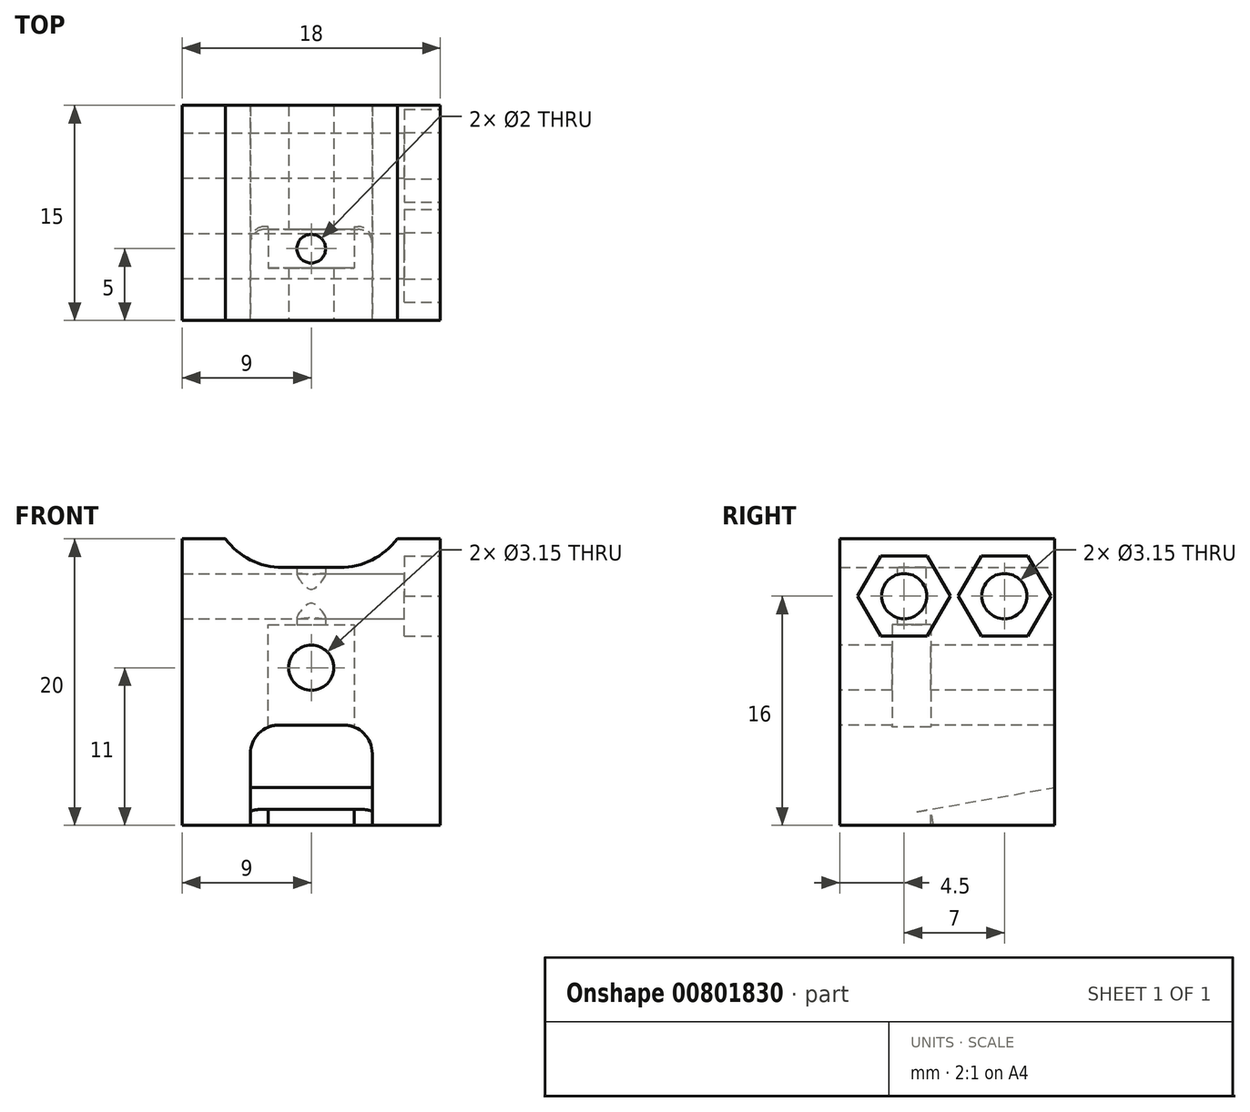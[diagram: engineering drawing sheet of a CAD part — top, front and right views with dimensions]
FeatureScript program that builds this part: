
annotation { "Feature Type Name" : "Feature", "Feature Type Description" : "" }
export const myFeature = defineFeature(function(context is Context, id is Id, definition is map)
    precondition{}
    {
        {
            var Q0;
            Q0=qCreatedBy(makeId("Front.planeOp"),FACE);
            var sketch = newSketch(context, id + "F0", { "sketchPlane" : qUnion([Q0])});
            skLineSegment(sketch, "E0.bottom", {"start": v(0, 0) * mm, "end": v(18, 0) * mm});
            skLineSegment(sketch, "E0.top", {"start": v(0, 20) * mm, "end": v(18, 20) * mm});
            skLineSegment(sketch, "E0.left", {"start": v(0, 0) * mm, "end": v(0, 20) * mm});
            skLineSegment(sketch, "E0.right", {"start": v(18, 0) * mm, "end": v(18, 20) * mm});
            skSolve(sketch);
        }
        {
            var Q0;
            Q0=makeQuery(id+"F0.imprint","IMPRINT",FACE,{"disambiguationData":[TD([[makeQuery(id+"F0.imprint","IMPRINT",EDGE,{"derivedFrom":sQuery(id+"F0.wireOp",EDGE,"E0.bottom")}),1.0]])]});
            extrude(context, id + "F1", {"entities" : qUnion([Q0]), "depth" : 15 * mm, "offsetDistance" : 25 * mm});
        }
        {
            var Q0;
            Q0=makeQuery(id+"F1.opExtrude","SWEPT_FACE",FACE,{"disambiguationData":[OSD([sQuery(id+"F0.wireOp",EDGE,"E0.right")])]});
            var sketch = newSketch(context, id + "F2", { "sketchPlane" : qUnion([Q0])});
            skPoint(sketch, "E1", {"position": v(-10.5, 16) * mm});
            skPoint(sketch, "E2", {"position": v(-3.5, 16) * mm});
            skSolve(sketch);
        }
        {
            var Q0;
            Q0=sQuery(id+"F2.wireOp",VERTEX,"E2");
            var Q1;
            Q1=sQuery(id+"F2.wireOp",VERTEX,"E1");
            var Q2;
            Q2=makeQuery(id+"F1.opExtrude","SWEPT_BODY",BODY,{"disambiguationData":[OSD([sQuery(id+"F0.wireOp",EDGE,"E0.bottom"),sQuery(id+"F0.wireOp",EDGE,"E0.top"),sQuery(id+"F0.wireOp",EDGE,"E0.left"),sQuery(id+"F0.wireOp",EDGE,"E0.right")])]});
            hole(context, id + "F3", {"style" : HoleStyle.SIMPLE, "endStyle" : HoleEndStyle.THROUGH, "standardTappedOrClearance" : lookupTablePath({ "standard" : "ISO", "fit" : "Close", "size" : "M3", "type" : "Clearance" }), "standardBlindInLast" : lookupTablePath({ "fit" : "Close", "standard" : "ISO", "size" : "M3", "type" : "Clearance" }), "holeDiameter" : 3.15 * mm, "majorDiameter" : 5 * mm, "isTappedThrough" : true, "tappedDepth" : 12 * mm, "tapClearance" : 3, "locations" : qUnion([Q0, Q1]), "scope" : qUnion([Q2])});
        }
        {
            var Q0;
            Q0=makeQuery(id+"F1.opExtrude","SWEPT_FACE",FACE,{"disambiguationData":[OSD([sQuery(id+"F0.wireOp",EDGE,"E0.right")])]});
            var sketch = newSketch(context, id + "F4", { "sketchPlane" : qUnion([Q0])});
            skCircle(sketch, "E3.cCircle", {"center": v(-10.5, 16) * mm, "radius": 2.8 * mm, "construction": true});
            skLineSegment(sketch, "E3.0", {"start": v(-7.27, 16) * mm, "end": v(-8.88, 13.2) * mm});
            skLineSegment(sketch, "E3.1", {"start": v(-8.88, 13.2) * mm, "end": v(-12.12, 13.2) * mm});
            skLineSegment(sketch, "E3.2", {"start": v(-12.12, 13.2) * mm, "end": v(-13.73, 16) * mm});
            skLineSegment(sketch, "E3.3", {"start": v(-13.73, 16) * mm, "end": v(-12.12, 18.8) * mm});
            skLineSegment(sketch, "E3.4", {"start": v(-12.12, 18.8) * mm, "end": v(-8.88, 18.8) * mm});
            skLineSegment(sketch, "E3.5", {"start": v(-8.88, 18.8) * mm, "end": v(-7.27, 16) * mm});
            skPoint(sketch, "E3.0.midPoint", {"position": v(-8.08, 14.6) * mm});
            skCircle(sketch, "E4.cCircle", {"center": v(-3.5, 16) * mm, "radius": 2.8 * mm, "construction": true});
            skLineSegment(sketch, "E4.0", {"start": v(-5.12, 13.2) * mm, "end": v(-6.73, 16) * mm});
            skLineSegment(sketch, "E4.1", {"start": v(-6.73, 16) * mm, "end": v(-5.12, 18.8) * mm});
            skLineSegment(sketch, "E4.2", {"start": v(-5.12, 18.8) * mm, "end": v(-1.88, 18.8) * mm});
            skLineSegment(sketch, "E4.3", {"start": v(-1.88, 18.8) * mm, "end": v(-0.27, 16) * mm});
            skLineSegment(sketch, "E4.4", {"start": v(-0.27, 16) * mm, "end": v(-1.88, 13.2) * mm});
            skLineSegment(sketch, "E4.5", {"start": v(-1.88, 13.2) * mm, "end": v(-5.12, 13.2) * mm});
            skPoint(sketch, "E4.0.midPoint", {"position": v(-5.92, 14.6) * mm});
            skSolve(sketch);
        }
        {
            var Q0;
            Q0=makeQuery(id+"F4.imprint","IMPRINT",FACE,{"disambiguationData":[TD([[makeQuery(id+"F4.imprint","IMPRINT",EDGE,{"derivedFrom":sQuery(id+"F4.wireOp",EDGE,"E3.0")}),-1.0]])]});
            var Q1;
            Q1=makeQuery(id+"F4.imprint","IMPRINT",FACE,{"disambiguationData":[TD([[makeQuery(id+"F4.imprint","IMPRINT",EDGE,{"derivedFrom":sQuery(id+"F4.wireOp",EDGE,"E4.0")}),-1.0]])]});
            extrude(context, id + "F5", {"entities" : qUnion([Q0, Q1]), "operationType" : NewBodyOperationType.REMOVE, "oppositeDirection" : true, "depth" : 2.5 * mm, "offsetDistance" : 25 * mm});
        }
        {
            var Q0;
            Q0=makeQuery(id+"F1.opExtrude","CAP_FACE",FACE,{"disambiguationData":[OSD([sQuery(id+"F0.wireOp",EDGE,"E0.bottom"),sQuery(id+"F0.wireOp",EDGE,"E0.top"),sQuery(id+"F0.wireOp",EDGE,"E0.left"),sQuery(id+"F0.wireOp",EDGE,"E0.right")])],"isStart":false});
            var sketch = newSketch(context, id + "F6", { "sketchPlane" : qUnion([Q0])});
            skLineSegment(sketch, "E5.bottom", {"start": v(4.75, 0) * mm, "end": v(13.25, 0) * mm});
            skLineSegment(sketch, "E5.top", {"start": v(4.75, 7) * mm, "end": v(13.25, 7) * mm});
            skLineSegment(sketch, "E5.left", {"start": v(4.75, 0) * mm, "end": v(4.75, 7) * mm});
            skLineSegment(sketch, "E5.right", {"start": v(13.25, 0) * mm, "end": v(13.25, 7) * mm});
            skSolve(sketch);
        }
        {
            var Q0;
            Q0 = qSketchRegion(id + "F6", true);
            extrude(context, id + "F7", {"entities" : qUnion([Q0]), "operationType" : NewBodyOperationType.REMOVE, "oppositeDirection" : true, "depth" : 15 * mm, "offsetDistance" : 25 * mm});
        }
        {
            var Q0;
            Q0=makeQuery(id+"F1.opExtrude","CAP_FACE",FACE,{"disambiguationData":[OSD([sQuery(id+"F0.wireOp",EDGE,"E0.bottom"),sQuery(id+"F0.wireOp",EDGE,"E0.top"),sQuery(id+"F0.wireOp",EDGE,"E0.left"),sQuery(id+"F0.wireOp",EDGE,"E0.right")])],"isStart":false});
            var sketch = newSketch(context, id + "F8", { "sketchPlane" : qUnion([Q0])});
            skPoint(sketch, "E6", {"position": v(9, 11) * mm});
            skSolve(sketch);
        }
        {
            var Q0;
            Q0=sQuery(id+"F8.wireOp",VERTEX,"E6");
            var Q1;
            Q1=makeQuery(id+"F1.opExtrude","SWEPT_BODY",BODY,{"disambiguationData":[OSD([sQuery(id+"F0.wireOp",EDGE,"E0.bottom"),sQuery(id+"F0.wireOp",EDGE,"E0.top"),sQuery(id+"F0.wireOp",EDGE,"E0.left"),sQuery(id+"F0.wireOp",EDGE,"E0.right")])]});
            hole(context, id + "F9", {"style" : HoleStyle.SIMPLE, "endStyle" : HoleEndStyle.THROUGH, "standardTappedOrClearance" : lookupTablePath({ "standard" : "ISO", "fit" : "Close", "size" : "M3", "type" : "Clearance" }), "standardBlindInLast" : lookupTablePath({ "fit" : "Close", "standard" : "ISO", "size" : "M3", "type" : "Clearance" }), "holeDiameter" : 3.15 * mm, "majorDiameter" : 5 * mm, "isTappedThrough" : true, "tappedDepth" : 12 * mm, "tapClearance" : 3, "locations" : qUnion([Q0]), "scope" : qUnion([Q1])});
        }
        {
            var Q0;
            Q0=makeQuery(id+"F1.opExtrude","CAP_FACE",FACE,{"disambiguationData":[OSD([sQuery(id+"F0.wireOp",EDGE,"E0.bottom"),sQuery(id+"F0.wireOp",EDGE,"E0.top"),sQuery(id+"F0.wireOp",EDGE,"E0.left"),sQuery(id+"F0.wireOp",EDGE,"E0.right")])],"isStart":false});
            cPlane(context, id + "F10", {"entities" : qUnion([Q0]), "cplaneType" : CPlaneType.OFFSET, "offset" : 5 * mm, "oppositeDirection" : true, "width" : 150 * mm, "height" : 150 * mm});
        }
        {
            var Q0;
            Q0=makeQuery(id+"F7.boolean.opBoolean","COPY",FACE,{"derivedFrom":makeQuery(id+"F7.opExtrude","SWEPT_FACE",FACE,{"disambiguationData":[OSD([sQuery(id+"F6.wireOp",EDGE,"E5.left")])]})});
            var sketch = newSketch(context, id + "F11", { "sketchPlane" : qUnion([Q0])});
            skLineSegment(sketch, "E7", {"start": v(-15, 0) * mm, "end": v(0, 2.64) * mm});
            skSolve(sketch);
        }
        {
            var Q0;
            {var subQ0=sQuery(id+"F11.wireOp",EDGE,"E7");Q0=makeQuery(id+"F11.imprint","IMPRINT",FACE,{"disambiguationData":[TD([[makeQuery(id+"F11.imprint","IMPRINT",EDGE,{"derivedFrom":subQ0}),-1.0]])]});}
            extrude(context, id + "F12", {"entities" : qUnion([Q0]), "operationType" : NewBodyOperationType.ADD, "endBound" : BoundingType.UP_TO_NEXT, "depth" : 25 * mm, "offsetDistance" : 25 * mm});
        }
        {
            var Q0;
            Q0=qCreatedBy(id+"F10.planeOp",FACE);
            var sketch = newSketch(context, id + "F13", { "sketchPlane" : qUnion([Q0])});
            skCircle(sketch, "E8.cCircle", {"center": v(9, 11) * mm, "radius": 3 * mm, "construction": true});
            skLineSegment(sketch, "E8.0", {"start": v(12, 14) * mm, "end": v(12, 8) * mm});
            skLineSegment(sketch, "E8.1", {"start": v(12, 8) * mm, "end": v(6, 8) * mm});
            skLineSegment(sketch, "E8.2", {"start": v(6, 8) * mm, "end": v(6, 14) * mm});
            skLineSegment(sketch, "E8.3", {"start": v(6, 14) * mm, "end": v(12, 14) * mm});
            skPoint(sketch, "E8.0.midPoint", {"position": v(12, 11) * mm});
            skLineSegment(sketch, "E9.bottom", {"start": v(6, 8) * mm, "end": v(12, 8) * mm});
            skLineSegment(sketch, "E9.top", {"start": v(6, 0) * mm, "end": v(12, 0) * mm});
            skLineSegment(sketch, "E9.left", {"start": v(6, 8) * mm, "end": v(6, 0) * mm});
            skLineSegment(sketch, "E9.right", {"start": v(12, 8) * mm, "end": v(12, 0) * mm});
            skSolve(sketch);
        }
        {
            var Q0;
            Q0=makeQuery(id+"F1.opExtrude","CAP_FACE",FACE,{"disambiguationData":[OSD([sQuery(id+"F0.wireOp",EDGE,"E0.bottom"),sQuery(id+"F0.wireOp",EDGE,"E0.top"),sQuery(id+"F0.wireOp",EDGE,"E0.left"),sQuery(id+"F0.wireOp",EDGE,"E0.right")])],"isStart":false});
            var sketch = newSketch(context, id + "F14", { "sketchPlane" : qUnion([Q0])});
            skLineSegment(sketch, "E10.bottom", {"start": v(3, 20) * mm, "end": v(15, 20) * mm});
            skLineSegment(sketch, "E10.top", {"start": v(3, 18) * mm, "end": v(15, 18) * mm});
            skLineSegment(sketch, "E10.left", {"start": v(3, 20) * mm, "end": v(3, 18) * mm});
            skLineSegment(sketch, "E10.right", {"start": v(15, 20) * mm, "end": v(15, 18) * mm});
            skSolve(sketch);
        }
        {
            var Q0;
            Q0=makeQuery(id+"F14.imprint","IMPRINT",FACE,{"disambiguationData":[TD([[makeQuery(id+"F14.imprint","IMPRINT",EDGE,{"derivedFrom":sQuery(id+"F14.wireOp",EDGE,"E10.bottom")}),-1.0]])]});
            extrude(context, id + "F15", {"entities" : qUnion([Q0]), "operationType" : NewBodyOperationType.REMOVE, "endBound" : BoundingType.THROUGH_ALL, "oppositeDirection" : true, "depth" : 25 * mm, "offsetDistance" : 25 * mm});
        }
        {
            var Q0;
            Q0 = qSketchRegion(id + "F13", true);
            extrude(context, id + "F16", {"entities" : qUnion([Q0]), "operationType" : NewBodyOperationType.REMOVE, "endBound" : BoundingType.SYMMETRIC, "oppositeDirection" : true, "depth" : 2.7 * mm, "offsetDistance" : 25 * mm});
        }
        {
            var Q0;
            Q0=makeQuery(id+"F16.boolean.opBoolean","COPY",FACE,{"derivedFrom":makeQuery(id+"F16.opExtrude","SWEPT_FACE",FACE,{"disambiguationData":[OSD([sQuery(id+"F13.wireOp",EDGE,"E8.3")])]})});
            var sketch = newSketch(context, id + "F17", { "sketchPlane" : qUnion([Q0])});
            skCircle(sketch, "E11", {"center": v(9, 10) * mm, "radius": 1 * mm});
            skLineSegment(sketch, "E12", {"start": v(9, 11.35) * mm, "end": v(9, 8.65) * mm, "construction": true});
            skLineSegment(sketch, "E13", {"start": v(6, 10) * mm, "end": v(12, 10) * mm, "construction": true});
            skSolve(sketch);
        }
        {
            var Q0;
            Q0=makeQuery(id+"F15.boolean.opBoolean","COPY",EDGE,{"derivedFrom":makeQuery(id+"F15.opExtrude","SWEPT_EDGE",EDGE,{"disambiguationData":[OSD([sQuery(id+"F14.wireOp",EDGE,"E10.top"),sQuery(id+"F14.wireOp",EDGE,"E10.left")])]})});
            var Q1;
            Q1=makeQuery(id+"F15.boolean.opBoolean","COPY",EDGE,{"derivedFrom":makeQuery(id+"F15.opExtrude","SWEPT_EDGE",EDGE,{"disambiguationData":[OSD([sQuery(id+"F14.wireOp",EDGE,"E10.top"),sQuery(id+"F14.wireOp",EDGE,"E10.right")])]})});
            fillet(context, id + "F18", {"entities" : qUnion([Q0, Q1]), "radius" : 5 * mm, "tangentPropagation" : true, "allowEdgeOverflow" : false});
        }
        {
            var Q0;
            Q0 = qSketchRegion(id + "F17", true);
            extrude(context, id + "F19", {"entities" : qUnion([Q0]), "operationType" : NewBodyOperationType.REMOVE, "endBound" : BoundingType.SYMMETRIC, "oppositeDirection" : true, "depth" : 50 * mm, "offsetDistance" : 25 * mm});
        }
        {
            var Q0;
            Q0=makeQuery(id+"F7.boolean.opBoolean","COPY",EDGE,{"derivedFrom":makeQuery(id+"F7.opExtrude","SWEPT_EDGE",EDGE,{"disambiguationData":[OSD([sQuery(id+"F6.wireOp",EDGE,"E5.top"),sQuery(id+"F6.wireOp",EDGE,"E5.left")])]})});
            var Q1;
            Q1=makeQuery(id+"F7.boolean.opBoolean","COPY",EDGE,{"derivedFrom":makeQuery(id+"F7.opExtrude","SWEPT_EDGE",EDGE,{"disambiguationData":[OSD([sQuery(id+"F6.wireOp",EDGE,"E5.top"),sQuery(id+"F6.wireOp",EDGE,"E5.right")])]})});
            var Q2;
            Q2=makeQuery(id+"F7.boolean.opBoolean","COPY",EDGE,{"derivedFrom":makeQuery(id+"F7.opExtrude","CAP_EDGE",EDGE,{"disambiguationData":[OSD([sQuery(id+"F6.wireOp",EDGE,"E5.top")])],"isStart":true})});
            fillet(context, id + "F20", {"entities" : qUnion([Q0, Q1, Q2]), "radius" : 2 * mm, "tangentPropagation" : true, "allowEdgeOverflow" : false});
        }
        {
            var Q0;
            Q0=makeQuery(id+"F12.opExtrude","SWEPT_FACE",FACE,{"disambiguationData":[OSD([sQuery(id+"F11.wireOp",EDGE,"E7")])]});
            var sketch = newSketch(context, id + "F21", { "sketchPlane" : qUnion([Q0])});
            skLineSegment(sketch, "E14.0.0", {"start": v(2.75, -14.77) * mm, "end": v(15.25, -14.77) * mm});
            skEllipticalArc(sketch, "E14.0.1", {});
            skLineSegment(sketch, "E14.0.2", {"start": v(13.25, -12.74) * mm, "end": v(13.25, 0.46) * mm});
            skLineSegment(sketch, "E14.0.3", {"start": v(13.25, 0.46) * mm, "end": v(4.75, 0.46) * mm});
            skLineSegment(sketch, "E14.0.4", {"start": v(4.75, 0.46) * mm, "end": v(4.75, -12.74) * mm});
            skEllipticalArc(sketch, "E14.0.5", {});
            skLineSegment(sketch, "E15", {"start": v(13.25, -11.07) * mm, "end": v(4.75, -11.07) * mm});
            skLineSegment(sketch, "E16.bottom", {"start": v(12, -8.32) * mm, "end": v(12.25, -8.32) * mm});
            skLineSegment(sketch, "E16.top", {"start": v(12, -11.07) * mm, "end": v(13.25, -11.07) * mm});
            skLineSegment(sketch, "E16.left", {"start": v(12, -8.32) * mm, "end": v(12, -11.07) * mm});
            skLineSegment(sketch, "E16.right", {"start": v(13.25, -9.32) * mm, "end": v(13.25, -11.07) * mm});
            skLineSegment(sketch, "E17.bottom", {"start": v(6, -8.32) * mm, "end": v(5.75, -8.32) * mm});
            skLineSegment(sketch, "E17.top", {"start": v(6, -11.07) * mm, "end": v(4.75, -11.07) * mm});
            skLineSegment(sketch, "E17.left", {"start": v(6, -8.32) * mm, "end": v(6, -11.07) * mm});
            skLineSegment(sketch, "E17.right", {"start": v(4.75, -9.32) * mm, "end": v(4.75, -11.07) * mm});
            skPoint(sketch, "E18.visualSharp", {"position": v(4.75, -8.32) * mm});
            skArc(sketch, "E18.filletArc", {"start": v(5.75, -8.32) * mm, "mid": v(5.04, -8.62) * mm, "end": v(4.75, -9.32) * mm});
            skPoint(sketch, "E19.visualSharp", {"position": v(13.25, -8.32) * mm});
            skArc(sketch, "E19.filletArc", {"start": v(13.25, -9.32) * mm, "mid": v(12.96, -8.62) * mm, "end": v(12.25, -8.32) * mm});
            skLineSegment(sketch, "E20", {"start": v(6, -8.32) * mm, "end": v(12, -8.32) * mm});
            const initialGuessF21  = {"E14.0.1": [0.01525, -0.012741263071411631, 0, -1, 0.00203085322377149, 0.002, 4.71238898038469, 0], "E14.0.5": [0.00275, -0.012741263071411631, 0, 1, 0.00203085322377149, 0.002, 3.141592653589793, 4.71238898038469]};
            skSetInitialGuess(sketch, initialGuessF21);
            skSolve(sketch);
        }
        {
            var Q0;
            Q0=makeQuery(id+"F21.imprint","IMPRINT",FACE,{"disambiguationData":[TD([[makeQuery(id+"F21.imprint","IMPRINT",EDGE,{"derivedFrom":sQuery(id+"F21.wireOp",EDGE,"E14.0.0")}),-1.0]])]});
            var Q1;
            Q1=makeQuery(id+"F21.imprint","IMPRINT",FACE,{"disambiguationData":[TD([[makeQuery(id+"F21.imprint","IMPRINT",EDGE,{"derivedFrom":sQuery(id+"F21.wireOp",EDGE,"E17.bottom")}),1.0]])]});
            var Q2;
            Q2=makeQuery(id+"F21.imprint","IMPRINT",FACE,{"disambiguationData":[TD([[makeQuery(id+"F21.imprint","IMPRINT",EDGE,{"derivedFrom":sQuery(id+"F21.wireOp",EDGE,"E16.bottom")}),-1.0]])]});
            var Q3;
            Q3=makeQuery(id+"F21.imprint","IMPRINT",FACE,{"disambiguationData":[TD([[makeQuery(id+"F21.imprint","IMPRINT",EDGE,{"derivedFrom":sQuery(id+"F21.wireOp",EDGE,"E15")}),1.0]])]});
            extrude(context, id + "F22", {"entities" : qUnion([Q0, Q1, Q2, Q3]), "operationType" : NewBodyOperationType.REMOVE, "endBound" : BoundingType.THROUGH_ALL, "oppositeDirection" : true, "depth" : 25 * mm, "offsetDistance" : 25 * mm});
        }
    });
